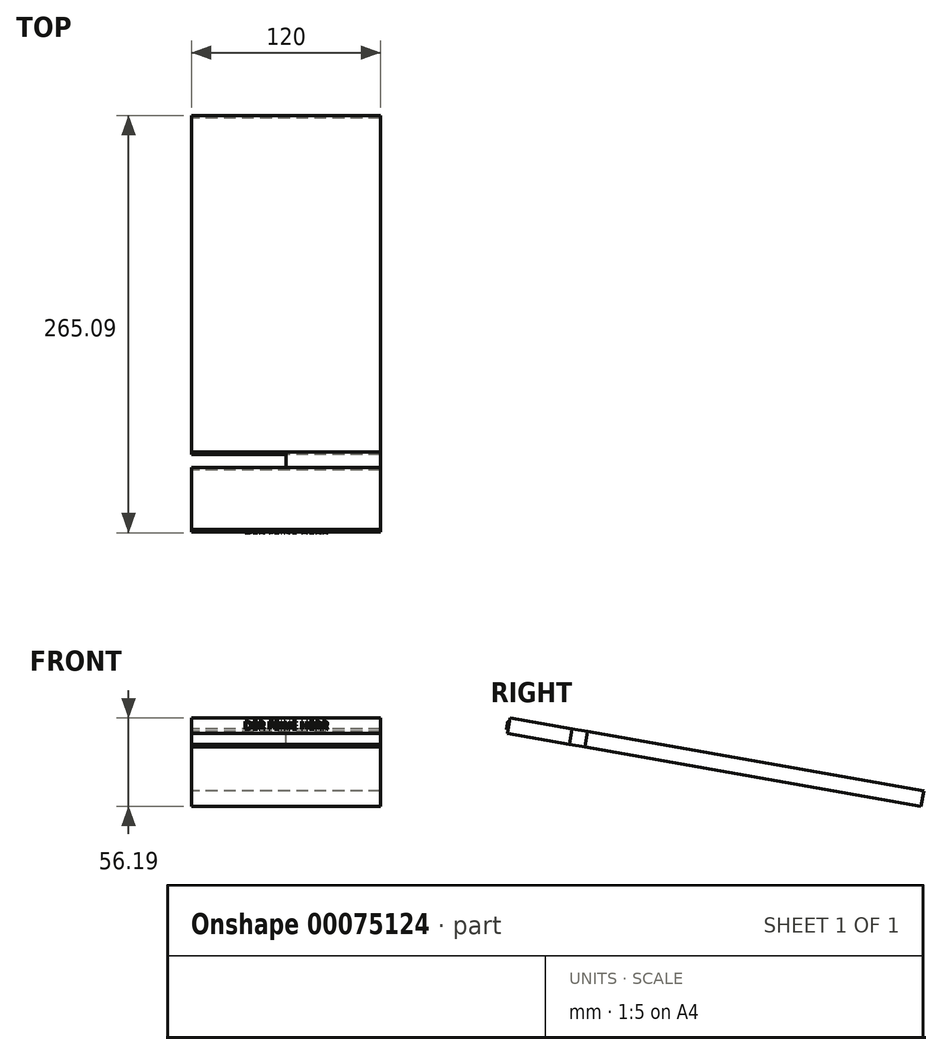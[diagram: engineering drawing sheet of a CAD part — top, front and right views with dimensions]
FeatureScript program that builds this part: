
annotation { "Feature Type Name" : "Feature", "Feature Type Description" : "" }
export const myFeature = defineFeature(function(context is Context, id is Id, definition is map)
    precondition{}
    {
        {
            var Q0;
            Q0=qCreatedBy(makeId("Right.planeOp"),FACE);
            var sketch = newSketch(context, id + "F0", { "sketchPlane" : qUnion([Q0])});
            skLineSegment(sketch, "E0", {"start": v(6.95, -77.7) * mm, "end": v(8.68, -67.86) * mm});
            skLineSegment(sketch, "E1", {"start": v(16.8, -79.45) * mm, "end": v(18.53, -69.6) * mm});
            skLineSegment(sketch, "E2", {"start": v(-30.7, -60.91) * mm, "end": v(232.09, -107.25) * mm});
            skLineSegment(sketch, "E3", {"start": v(230.35, -117.1) * mm, "end": v(-32.45, -70.76) * mm});
            skLineSegment(sketch, "E4", {"start": v(-32.45, -70.76) * mm, "end": v(-30.7, -60.91) * mm});
            skLineSegment(sketch, "E5", {"start": v(230.35, -117.1) * mm, "end": v(232.09, -107.25) * mm});
            skSolve(sketch);
        }
        {
            var Q0;
            {var subQ0=sQuery(id+"F0.wireOp",EDGE,"E0");Q0=makeQuery(id+"F0.imprint","IMPRINT",FACE,{"disambiguationData":[TD([[makeQuery(id+"F0.imprint","IMPRINT",EDGE,{"derivedFrom":subQ0}),1.0]])]});}
            var Q1;
            {var subQ0=sQuery(id+"F0.wireOp",EDGE,"E1");Q1=makeQuery(id+"F0.imprint","IMPRINT",FACE,{"disambiguationData":[TD([[makeQuery(id+"F0.imprint","IMPRINT",EDGE,{"derivedFrom":subQ0}),-1.0]])]});}
            extrude(context, id + "F1", {"entities" : qUnion([Q0, Q1]), "endBound" : BoundingType.SYMMETRIC, "depth" : 120 * mm});
        }
        {
            var Q0;
            {var subQ0=sQuery(id+"F0.wireOp",EDGE,"E0");Q0=makeQuery(id+"F0.imprint","IMPRINT",FACE,{"disambiguationData":[TD([[makeQuery(id+"F0.imprint","IMPRINT",EDGE,{"derivedFrom":subQ0}),-1.0]])]});}
            extrude(context, id + "F2", {"entities" : qUnion([Q0]), "depth" : 60 * mm});
        }
        {
            var Q0;
            Q0=makeQuery(id+"F1.opExtrude","SWEPT_FACE",FACE,{"disambiguationData":[OSD([sQuery(id+"F0.wireOp",EDGE,"E4")])]});
            var sketch = newSketch(context, id + "F3", { "sketchPlane" : qUnion([Q0])});
            skText(sketch, "E6", { "text": "DER FEINE HERR", "fontName": "OpenSans-Regular.ttf"});
            const initialGuessF3  = {"E6": [-0.02675, -0.07286, 1, 0, 0.00507]};
            skSetInitialGuess(sketch, initialGuessF3);
            skSolve(sketch);
        }
        {
            var Q0;
            Q0 = qSketchRegion(id + "F3", true);
            extrude(context, id + "F4", {"entities" : qUnion([Q0]), "operationType" : NewBodyOperationType.ADD, "depth" : 1 * mm});
        }
    });
